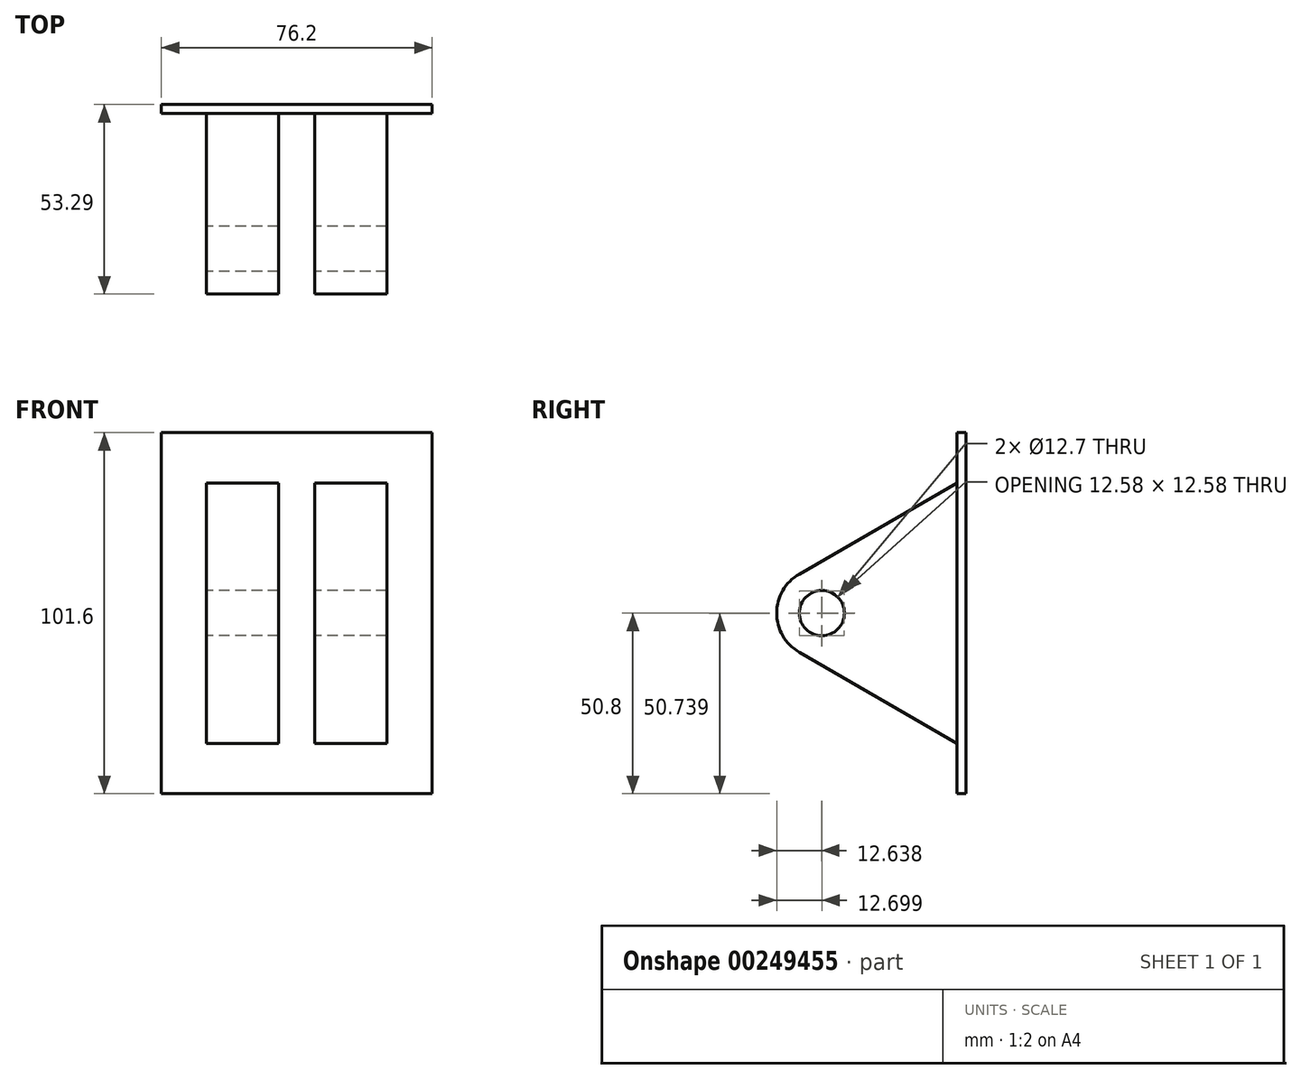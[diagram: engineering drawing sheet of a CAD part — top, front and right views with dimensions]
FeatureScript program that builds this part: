
annotation { "Feature Type Name" : "Feature", "Feature Type Description" : "" }
export const myFeature = defineFeature(function(context is Context, id is Id, definition is map)
    precondition{}
    {
        {
            var Q0;
            Q0=qCreatedBy(makeId("Front.planeOp"),FACE);
            var sketch = newSketch(context, id + "F0", { "sketchPlane" : qUnion([Q0])});
            skLineSegment(sketch, "E0.bottom", {"start": v(-38.1, 50.8) * mm, "end": v(38.1, 50.8) * mm});
            skLineSegment(sketch, "E0.top", {"start": v(-38.1, -50.8) * mm, "end": v(38.1, -50.8) * mm});
            skLineSegment(sketch, "E0.left", {"start": v(-38.1, 50.8) * mm, "end": v(-38.1, -50.8) * mm});
            skLineSegment(sketch, "E0.right", {"start": v(38.1, 50.8) * mm, "end": v(38.1, -50.8) * mm});
            skPoint(sketch, "E1.middle", {"position": v(0, 0) * mm});
            skSolve(sketch);
        }
        {
            var Q0;
            Q0 = qSketchRegion(id + "F0", true);
            extrude(context, id + "F1", {"entities" : qUnion([Q0]), "offsetDistance" : 25.4 * mm, "depth" : 2.5 * mm});
        }
        {
            var Q0;
            Q0=qCreatedBy(makeId("Right.planeOp"),FACE);
            var sketch = newSketch(context, id + "F2", { "sketchPlane" : qUnion([Q0])});
            skLineSegment(sketch, "E2", {"start": v(0, -38.1) * mm, "end": v(-46.94, -11) * mm});
            skLineSegment(sketch, "E3", {"start": v(-46.94, 11) * mm, "end": v(0, 38.1) * mm});
            skLineSegment(sketch, "E4", {"start": v(0, 38.1) * mm, "end": v(0, -38.1) * mm});
            skArc(sketch, "E5", {"start": v(-46.94, 11) * mm, "mid": v(-53.3, 0) * mm, "end": v(-46.94, -11) * mm});
            skPoint(sketch, "E6.orphan", {"position": v(-66, 0) * mm});
            skCircle(sketch, "E7", {"center": v(-40.6, 0) * mm, "radius": 6.35 * mm});
            skSolve(sketch);
        }
        {
            var Q0;
            Q0=makeQuery(id+"F2.imprint","IMPRINT",FACE,{"disambiguationData":[TD([[makeQuery(id+"F2.imprint","IMPRINT",EDGE,{"derivedFrom":sQuery(id+"F2.wireOp",EDGE,"E2")}),-1.0]])]});
            extrude(context, id + "F3", {"entities" : qUnion([Q0]), "operationType" : NewBodyOperationType.ADD, "endBound" : BoundingType.SYMMETRIC, "depth" : 50.8 * mm});
        }
        {
            var Q0;
            Q0=qCreatedBy(makeId("Top.planeOp"),FACE);
            var sketch = newSketch(context, id + "F4", { "sketchPlane" : qUnion([Q0])});
            skLineSegment(sketch, "E8.top", {"start": v(-7.6, -101.42) * mm, "end": v(7.6, -101.42) * mm});
            skPoint(sketch, "E8.middle", {"position": v(0, -50.7) * mm});
            skPoint(sketch, "E8.bottom.end.orphan", {"position": v(7.6, 0) * mm});
            skPoint(sketch, "E8.bottom.start.orphan", {"position": v(-7.6, 0) * mm});
            skLineSegment(sketch, "E9.bottom", {"start": v(-5.09, -2.5) * mm, "end": v(5.09, -2.5) * mm});
            skLineSegment(sketch, "E9.top", {"start": v(-5.09, -104.1) * mm, "end": v(5.09, -104.1) * mm});
            skLineSegment(sketch, "E9.left", {"start": v(-5.09, -2.5) * mm, "end": v(-5.09, -104.1) * mm});
            skLineSegment(sketch, "E9.right", {"start": v(5.09, -2.5) * mm, "end": v(5.09, -104.1) * mm});
            skPoint(sketch, "E9.middle", {"position": v(0, -53.3) * mm});
            skSolve(sketch);
        }
        {
            var Q0;
            {var subQ5=sQuery(id+"F4.wireOp",EDGE,"E9.bottom");Q0=makeQuery(id+"F4.imprint","IMPRINT",FACE,{"disambiguationData":[TD([[makeQuery(id+"F4.imprint","IMPRINT",EDGE,{"derivedFrom":subQ5}),-1.0]])]});}
            extrude(context, id + "F5", {"entities" : qUnion([Q0]), "operationType" : NewBodyOperationType.REMOVE, "endBound" : BoundingType.SYMMETRIC, "oppositeDirection" : true, "depth" : 151.9 * mm});
        }
    });
